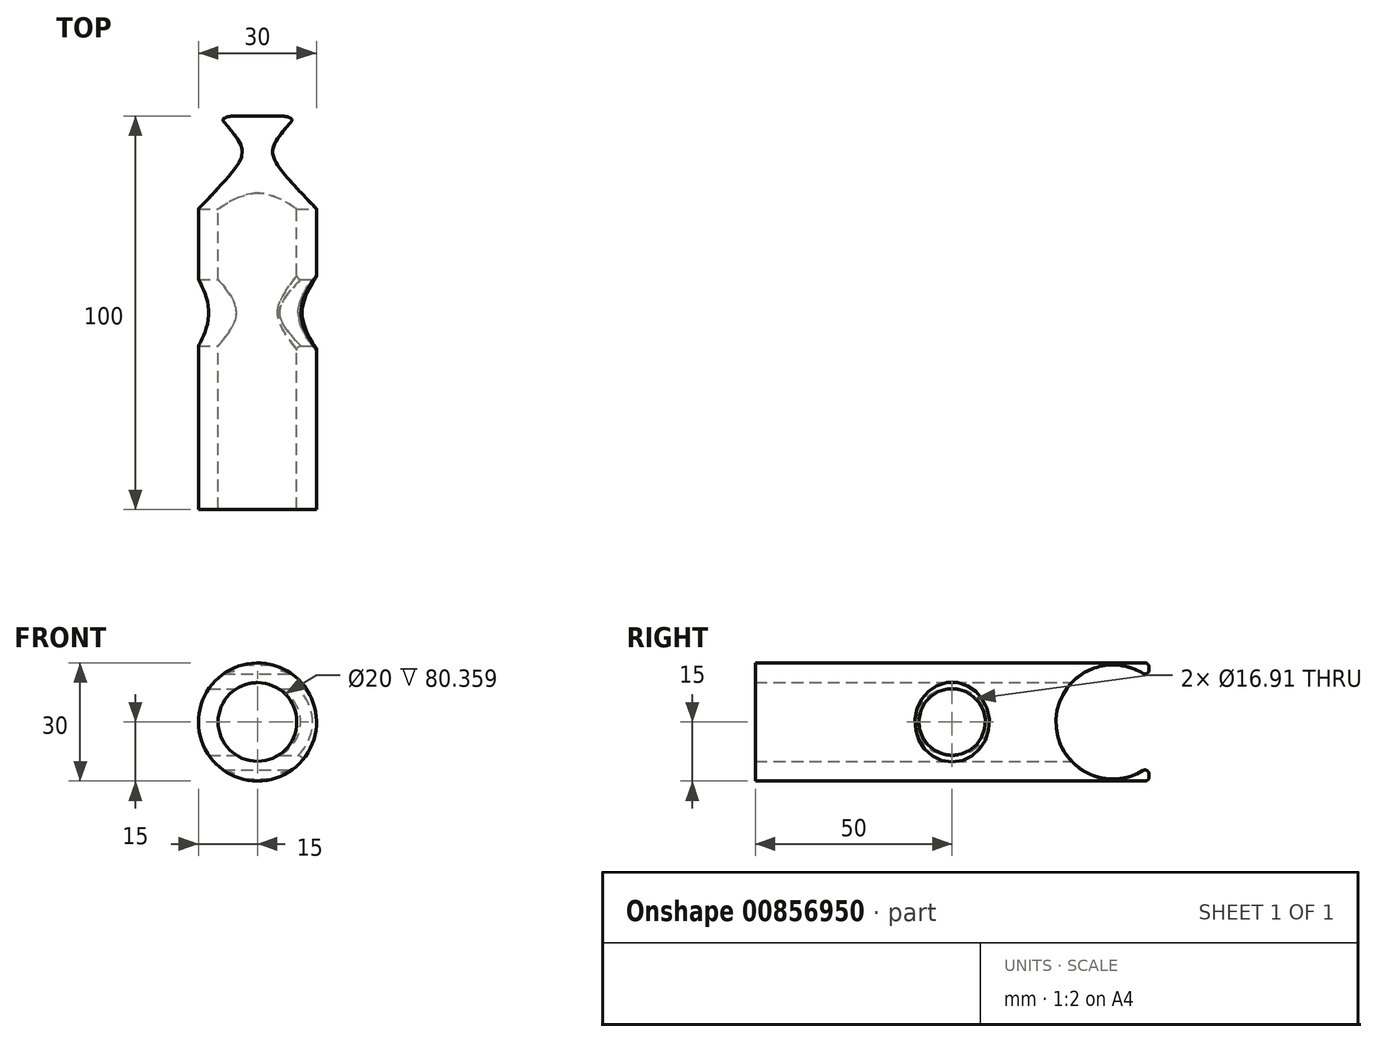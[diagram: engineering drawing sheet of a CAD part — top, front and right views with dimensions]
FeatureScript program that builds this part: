
annotation { "Feature Type Name" : "Feature", "Feature Type Description" : "" }
export const myFeature = defineFeature(function(context is Context, id is Id, definition is map)
    precondition{}
    {
        {
            var Q0;
            Q0=qCreatedBy(makeId("Front.planeOp"),FACE);
            var sketch = newSketch(context, id + "F0", { "sketchPlane" : qUnion([Q0])});
            skCircle(sketch, "E0", {"center": v(0, 0) * mm, "radius": 15 * mm});
            skCircle(sketch, "E1", {"center": v(0, 0) * mm, "radius": 10 * mm});
            skSolve(sketch);
        }
        {
            var Q0;
            Q0=makeQuery(id+"F0.imprint","IMPRINT",FACE,{"disambiguationData":[TD([[makeQuery(id+"F0.imprint","IMPRINT",EDGE,{"derivedFrom":sQuery(id+"F0.wireOp",EDGE,"E0")}),1.0]])]});
            extrude(context, id + "F1", {"entities" : qUnion([Q0]), "endBound" : BoundingType.SYMMETRIC, "depth" : 100 * mm, "offsetDistance" : 25 * mm});
        }
        {
            var Q0;
            Q0=qCreatedBy(makeId("Right.planeOp"),FACE);
            var sketch = newSketch(context, id + "F2", { "sketchPlane" : qUnion([Q0])});
            skCircle(sketch, "E2", {"center": v(0, 0) * mm, "radius": 8.45 * mm});
            skSolve(sketch);
        }
        {
            var Q0;
            Q0=makeQuery(id+"F2.imprint","IMPRINT",FACE,{"disambiguationData":[TD([[makeQuery(id+"F2.imprint","IMPRINT",EDGE,{"derivedFrom":sQuery(id+"F2.wireOp",EDGE,"E2")}),1.0]])]});
            extrude(context, id + "F3", {"entities" : qUnion([Q0]), "operationType" : NewBodyOperationType.REMOVE, "endBound" : BoundingType.SYMMETRIC, "oppositeDirection" : true, "depth" : 50 * mm, "offsetDistance" : 25 * mm});
        }
        {
            var Q0;
            Q0=qCreatedBy(makeId("Right.planeOp"),FACE);
            cPlane(context, id + "F4", {"entities" : qUnion([Q0]), "cplaneType" : CPlaneType.OFFSET, "offset" : 20 * mm, "width" : 150 * mm, "height" : 150 * mm});
        }
        {
            var Q0;
            Q0=qCreatedBy(id+"F4.planeOp",FACE);
            var sketch = newSketch(context, id + "F5", { "sketchPlane" : qUnion([Q0])});
            skCircle(sketch, "E3", {"center": v(40.85, 0) * mm, "radius": 14.5 * mm});
            skSolve(sketch);
        }
        {
            var Q0;
            Q0=makeQuery(id+"F5.imprint","IMPRINT",FACE,{"disambiguationData":[TD([[makeQuery(id+"F5.imprint","IMPRINT",EDGE,{"derivedFrom":sQuery(id+"F5.wireOp",EDGE,"E3")}),1.0]])]});
            extrude(context, id + "F6", {"entities" : qUnion([Q0]), "operationType" : NewBodyOperationType.REMOVE, "oppositeDirection" : true, "depth" : 50 * mm, "offsetDistance" : 25 * mm});
        }
        {
            var Q0;
            Q0=makeQuery(id+"F6.boolean.opBoolean","SPLIT",FACE,{"disambiguationData":[OD(0.0)],"derivedFrom":makeQuery(id+"F1.opExtrude","CAP_FACE",FACE,{"disambiguationData":[OSD([sQuery(id+"F0.wireOp",EDGE,"E0"),sQuery(id+"F0.wireOp",EDGE,"E1")])],"isStart":true})});
            var Q1;
            Q1=makeQuery(id+"F6.boolean.opBoolean","SPLIT",FACE,{"disambiguationData":[OD(1.0)],"derivedFrom":makeQuery(id+"F1.opExtrude","CAP_FACE",FACE,{"disambiguationData":[OSD([sQuery(id+"F0.wireOp",EDGE,"E0"),sQuery(id+"F0.wireOp",EDGE,"E1")])],"isStart":true})});
            var Q2;
            Q2=makeQuery(id+"F3.boolean.opBoolean","COPY",FACE,{"disambiguationData":[OD(1.0)],"derivedFrom":makeQuery(id+"F3.opExtrude","SWEPT_FACE",FACE,{"disambiguationData":[OSD([sQuery(id+"F2.wireOp",EDGE,"E2")])]})});
            fillet(context, id + "F7", {"entities" : qUnion([Q0, Q1, Q2]), "radius" : 1 * mm, "tangentPropagation" : true, "allowEdgeOverflow" : false});
        }
    });
